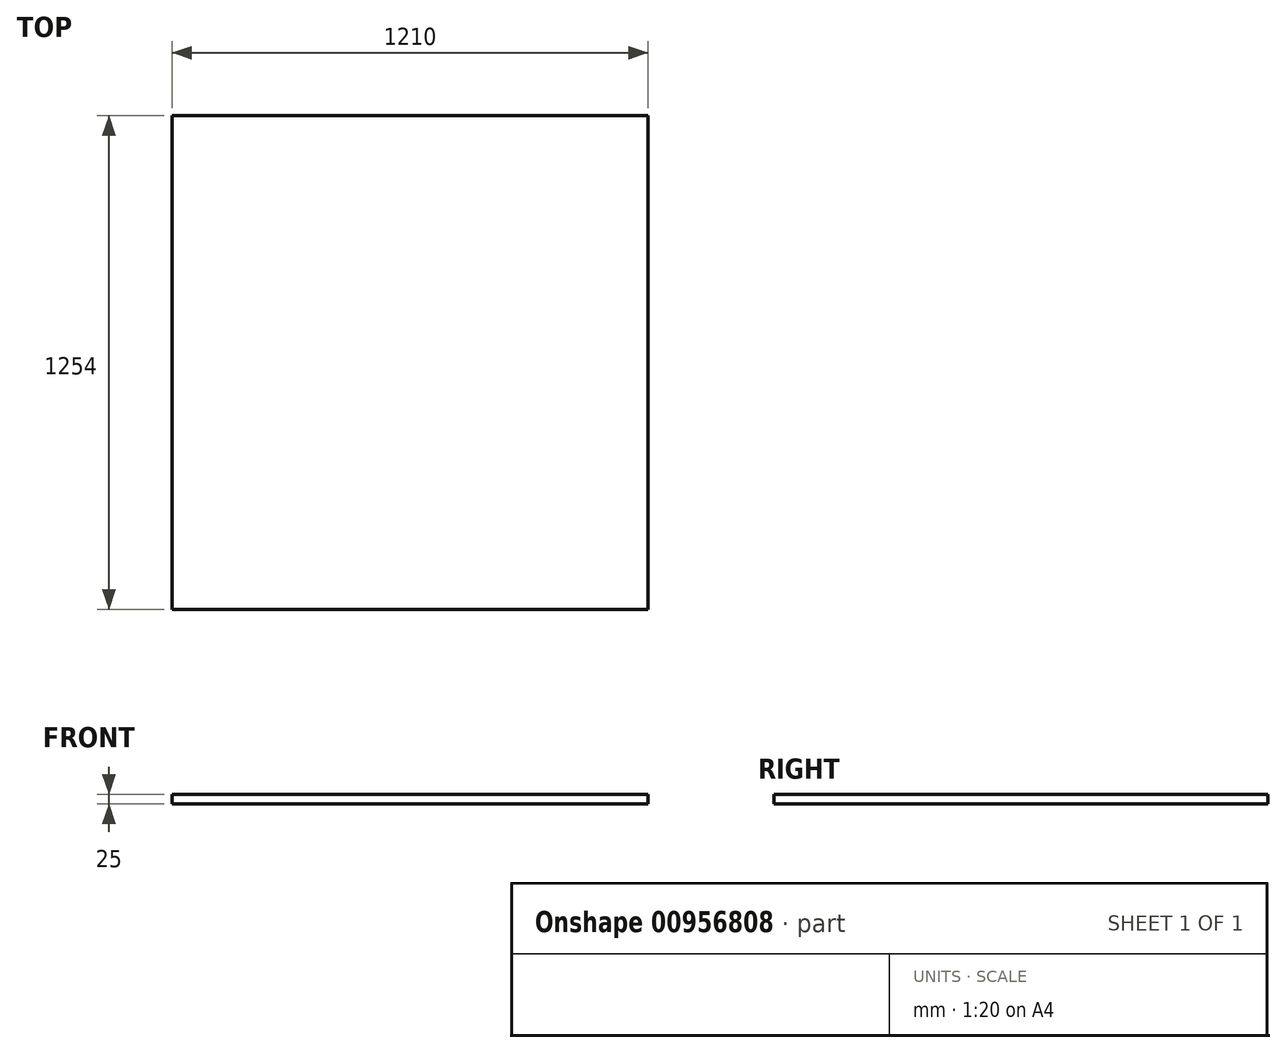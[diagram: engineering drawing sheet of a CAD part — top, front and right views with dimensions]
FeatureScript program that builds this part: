
annotation { "Feature Type Name" : "Feature", "Feature Type Description" : "" }
export const myFeature = defineFeature(function(context is Context, id is Id, definition is map)
    precondition{}
    {
        {
            var Q0;
            Q0=qCreatedBy(makeId("Top.planeOp"),FACE);
            var sketch = newSketch(context, id + "F0", { "sketchPlane" : qUnion([Q0])});
            skLineSegment(sketch, "E0.bottom", {"start": v(605, 627) * mm, "end": v(-605, 627) * mm});
            skLineSegment(sketch, "E0.top", {"start": v(605, -627) * mm, "end": v(-605, -627) * mm});
            skLineSegment(sketch, "E0.left", {"start": v(605, 627) * mm, "end": v(605, -627) * mm});
            skLineSegment(sketch, "E0.right", {"start": v(-605, 627) * mm, "end": v(-605, -627) * mm});
            skPoint(sketch, "E0.middle", {"position": v(0, 0) * mm});
            skSolve(sketch);
        }
        {
            var Q0;
            Q0 = qSketchRegion(id + "F0", true);
            extrude(context, id + "F1", {"entities" : qUnion([Q0]), "depth" : 25 * mm, "offsetDistance" : 25 * mm});
        }
    });
